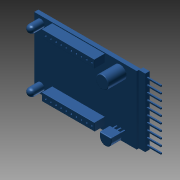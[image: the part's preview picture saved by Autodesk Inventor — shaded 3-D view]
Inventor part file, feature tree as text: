
AUTODESK INVENTOR PART (.ipt)
format: ipt  version: 2012 (Build 160160000, 160)  size: 471,552 bytes
history: native  units: in
note: dims shown in document units (in); Inventor stores cm internally (conversion verified against a paired STEP export)
features: extrude x9, fillet x4, sketch x3
ambient origin geometry x8: Origin, YZ Plane, XZ Plane, XY Plane, X Axis, Y Axis, Z Axis, Center Point
bodies: Solid1 (feature_tree)
feature tree (16):
  sketch  "Sketch1"  dims[d0=1.5748in d1=1.0433in]
  extrude  "Extrusion1"  Depth=1.0433in
  extrude  "Extrusion2"  Depth=0.1181in
  extrude  "Extrusion3"  Depth=0.1181in
  fillet  "Fillet1"  Radius=0.1181in
  fillet  "Fillet2"  Radius=0.0394in
  extrude  "Extrusion5"  Depth=0.0394in
  sketch  "Sketch3"  dims[d3=0.8071in d4=0.1181in]
  extrude  "Extrusion8"  Depth=0.1969in
  extrude  "Extrusion9"  Depth=0.1575in
  extrude  "Extrusion10"  Depth=0.0394in
  extrude  "Extrusion11"  Depth=0.063in TaperAngle=0.0deg
  fillet  "Fillet6"  Radius=0.2756in
  extrude  "Extrusion12"  Depth=0.1969in TaperAngle=0.0deg
  fillet  "Fillet7"  Radius=0.059in
  sketch  "Sketch4"  dims[d6=0.2756in d8=0.1181in d9=0.1181in d10=0.0394in d11=0.0394in d12=0.1969in d13=0.1575in d14=0.0394in d15=0.063in d16=0.0in d17=0.2756in d18=0.0in d19=0.1969in d20=0.0in d21=0.059in d22=0.01in d23=0.0591in d24=0.1772in d28=0.0394in d29=0.1575in d33=0.0197in d34=0.0197in d35=0.0197in d36=0.0197in d37=0.0197in d38=0.0197in d39=0.0394in d40=0.0394in d41=0.0197in d42=0.0197in d43=0.0197in d44=0.018in d45=0.0787in d46=0.0in d56=0.042in d58=0.042in d122=1.0433in d123=0.0669in d124=0.0197in d125=0.0197in d126=0.0615in d127=0.0236in d128=0.0197in d129=0.0197in d130=0.0197in d131=0.0197in d145=0.0236in d147=0.0236in d148=0.0197in d149=0.0197in d150=0.1in d151=0.0236in d152=0.1in d154=0.0197in d155=0.0197in d156=0.1in d157=0.0236in d158=0.0197in d159=0.0197in d160=0.1in d161=0.0236in d162=0.1in d163=0.0197in d164=0.0197in d166=0.1in d167=0.0236in d168=0.0197in d169=0.0197in d170=0.1in d171=0.0236in d172=0.0197in d173=0.0197in d174=0.1in d175=0.0236in d176=0.0197in d177=0.0197in d178=0.1in d179=0.0236in d180=0.315in d181=0.0in d182=0.0984in d183=0.0in d184=0.1181in d185=0.0in d191=0.0236in d192=0.0236in d193=0.043in d194=0.0472in d195=0.0236in d196=0.0236in d197=0.0787in d198=0.0472in d199=0.0236in d200=0.0236in d202=0.0472in d203=0.0236in d204=0.0236in d205=0.0787in d206=0.0787in d207=0.0787in d208=0.0236in d209=0.0236in d210=0.0472in d211=0.0236in d212=0.0236in d213=0.0787in d214=0.0472in d215=0.0236in d216=0.0236in d217=0.0787in d218=0.0472in d219=0.0236in d220=0.0236in d221=0.0787in d222=0.0472in d223=0.0236in d224=0.0236in d225=0.0787in d226=0.0472in d227=0.0236in d228=0.0236in d229=0.0787in d230=0.0472in d231=0.8071in d232=0.1181in d233=0.0236in d234=0.0236in d235=0.043in d236=0.0472in d237=0.0236in d238=0.0236in d239=0.0787in d240=0.0472in d241=0.0236in d242=0.0236in d243=0.0472in d244=0.0236in d245=0.0236in d246=0.0787in d247=0.0787in d248=0.0787in d249=0.0236in d250=0.0236in d251=0.0472in d252=0.0236in d253=0.0236in d254=0.0787in d255=0.0472in d256=0.0236in d257=0.0236in d258=0.0787in d259=0.0472in d260=0.0236in d261=0.0236in d262=0.0787in d263=0.0472in d264=0.0236in d265=0.0236in d266=0.0787in d267=0.0472in d268=0.0236in d269=0.0236in d270=0.0787in d271=0.0472in d274=0.7224in d275=0.2756in d276=0.1575in d277=0.0in d278=0.005in d279=0.1575in d280=0.0in d281=0.01in]
